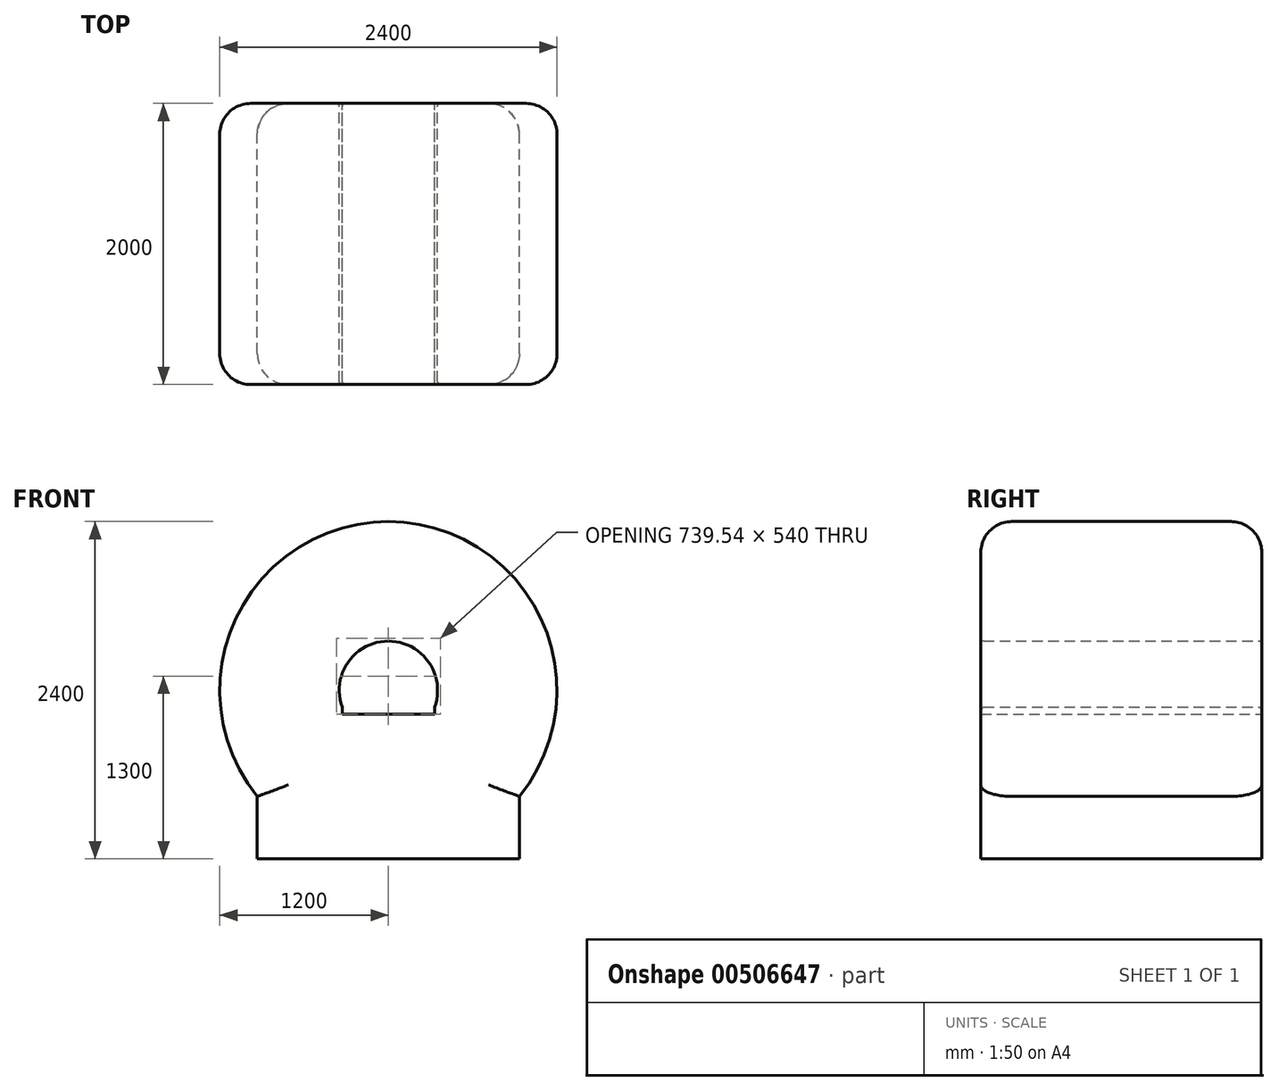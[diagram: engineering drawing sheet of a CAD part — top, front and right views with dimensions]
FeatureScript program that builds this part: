
annotation { "Feature Type Name" : "Feature", "Feature Type Description" : "" }
export const myFeature = defineFeature(function(context is Context, id is Id, definition is map)
    precondition{}
    {
        {
            var Q0;
            Q0=qCreatedBy(makeId("Front.planeOp"),FACE);
            var sketch = newSketch(context, id + "F0", { "sketchPlane" : qUnion([Q0])});
            skArc(sketch, "E0", {"start": v(932.57, -755.19) * mm, "mid": v(0, 1200) * mm, "end": v(-932.57, -755.19) * mm});
            skLineSegment(sketch, "E1", {"start": v(0, -1200) * mm, "end": v(0, -373.03) * mm, "construction": true});
            skLineSegment(sketch, "E2", {"start": v(0, -1200) * mm, "end": v(-932.57, -1200) * mm});
            skLineSegment(sketch, "E3", {"start": v(-932.57, -1200) * mm, "end": v(-932.57, -755.19) * mm});
            skLineSegment(sketch, "E4.MirrorCS", {"start": v(0, -1200) * mm, "end": v(932.57, -1200) * mm});
            skLineSegment(sketch, "E5.MirrorCS", {"start": v(932.57, -1200) * mm, "end": v(932.57, -755.19) * mm});
            skCircle(sketch, "E6", {"center": v(0, 0) * mm, "radius": 350 * mm});
            skSolve(sketch);
        }
        {
            var Q0;
            Q0 = qSketchRegion(id + "F0", true);
            extrude(context, id + "F1", {"entities" : qUnion([Q0]), "depth" : 2000 * mm});
        }
        {
            var Q0;
            Q0=makeQuery(id+"F1.opExtrude","CAP_EDGE",EDGE,{"disambiguationData":[OSD([sQuery(id+"F0.wireOp",EDGE,"E0")])],"isStart":false});
            var Q1;
            Q1=makeQuery(id+"F1.opExtrude","CAP_EDGE",EDGE,{"disambiguationData":[OSD([sQuery(id+"F0.wireOp",EDGE,"E0")])],"isStart":true});
            var Q2;
            Q2=makeQuery(id+"F1.opExtrude","CAP_EDGE",EDGE,{"disambiguationData":[OSD([sQuery(id+"F0.wireOp",EDGE,"E5.MirrorCS")])],"isStart":false});
            var Q3;
            Q3=makeQuery(id+"F1.opExtrude","CAP_EDGE",EDGE,{"disambiguationData":[OSD([sQuery(id+"F0.wireOp",EDGE,"E3")])],"isStart":false});
            var Q4;
            Q4=makeQuery(id+"F1.opExtrude","CAP_EDGE",EDGE,{"disambiguationData":[OSD([sQuery(id+"F0.wireOp",EDGE,"E5.MirrorCS")])],"isStart":true});
            var Q5;
            Q5=makeQuery(id+"F1.opExtrude","CAP_EDGE",EDGE,{"disambiguationData":[OSD([sQuery(id+"F0.wireOp",EDGE,"E3")])],"isStart":true});
            fillet(context, id + "F2", {"entities" : qUnion([Q0, Q1, Q2, Q3, Q4, Q5]), "radius" : 220 * mm, "tangentPropagation" : true, "allowEdgeOverflow" : false});
        }
        {
            var Q0;
            Q0=makeQuery(id+"F1.opExtrude","CAP_FACE",FACE,{"disambiguationData":[OSD([sQuery(id+"F0.wireOp",EDGE,"E0"),sQuery(id+"F0.wireOp",EDGE,"E2"),sQuery(id+"F0.wireOp",EDGE,"E3"),sQuery(id+"F0.wireOp",EDGE,"E4.MirrorCS"),sQuery(id+"F0.wireOp",EDGE,"E5.MirrorCS"),sQuery(id+"F0.wireOp",EDGE,"E6")])],"isStart":true});
            var sketch = newSketch(context, id + "F3", { "sketchPlane" : qUnion([Q0])});
            skLineSegment(sketch, "E7", {"start": v(0, 0) * mm, "end": v(0, -350) * mm, "construction": true});
            skLineSegment(sketch, "E8", {"start": v(0, -120) * mm, "end": v(-328.79, -120) * mm});
            skLineSegment(sketch, "E9", {"start": v(-328.79, -120) * mm, "end": v(-328.79, -170) * mm});
            skLineSegment(sketch, "E10", {"start": v(-328.79, -170) * mm, "end": v(0, -170) * mm});
            skLineSegment(sketch, "E11.MirrorCS", {"start": v(328.79, -170) * mm, "end": v(0, -170) * mm});
            skLineSegment(sketch, "E12.MirrorCS", {"start": v(328.79, -120) * mm, "end": v(328.79, -170) * mm});
            skLineSegment(sketch, "E13.MirrorCS", {"start": v(0, -120) * mm, "end": v(328.79, -120) * mm});
            skLineSegment(sketch, "E14", {"start": v(0, -120) * mm, "end": v(0, 350) * mm, "construction": true});
            skSolve(sketch);
        }
        {
            var Q0;
            Q0 = qSketchRegion(id + "F3", true);
            extrude(context, id + "F4", {"entities" : qUnion([Q0]), "operationType" : NewBodyOperationType.REMOVE, "endBound" : BoundingType.THROUGH_ALL, "oppositeDirection" : true, "depth" : 25 * mm});
        }
        {
            var Q0;
            Q0=makeQuery(id+"F1.opExtrude","CAP_FACE",FACE,{"disambiguationData":[OSD([sQuery(id+"F0.wireOp",EDGE,"E0"),sQuery(id+"F0.wireOp",EDGE,"E2"),sQuery(id+"F0.wireOp",EDGE,"E3"),sQuery(id+"F0.wireOp",EDGE,"E4.MirrorCS"),sQuery(id+"F0.wireOp",EDGE,"E5.MirrorCS"),sQuery(id+"F0.wireOp",EDGE,"E6")])],"isStart":true});
            var sketch = newSketch(context, id + "F5", { "sketchPlane" : qUnion([Q0])});
            skLineSegment(sketch, "E15", {"start": v(-305.94, -170) * mm, "end": v(305.94, -170) * mm});
            skLineSegment(sketch, "E16", {"start": v(0, -350) * mm, "end": v(287.25, -350) * mm});
            skLineSegment(sketch, "E17", {"start": v(287.25, -350) * mm, "end": v(305.94, -170) * mm});
            skLineSegment(sketch, "E18.MirrorCS", {"start": v(-287.25, -350) * mm, "end": v(-305.94, -170) * mm});
            skLineSegment(sketch, "E19.MirrorCS", {"start": v(0, -350) * mm, "end": v(-287.25, -350) * mm});
            skSolve(sketch);
        }
        {
            var Q0;
            Q0 = qSketchRegion(id + "F5", true);
            var Q1;
            Q1=makeQuery(id+"F1.opExtrude","CAP_FACE",FACE,{"disambiguationData":[OSD([sQuery(id+"F0.wireOp",EDGE,"E0"),sQuery(id+"F0.wireOp",EDGE,"E2"),sQuery(id+"F0.wireOp",EDGE,"E3"),sQuery(id+"F0.wireOp",EDGE,"E4.MirrorCS"),sQuery(id+"F0.wireOp",EDGE,"E5.MirrorCS"),sQuery(id+"F0.wireOp",EDGE,"E6")])],"isStart":false});
            extrude(context, id + "F6", {"entities" : qUnion([Q0]), "operationType" : NewBodyOperationType.ADD, "endBound" : BoundingType.UP_TO_SURFACE, "oppositeDirection" : true, "endBoundEntityFace" : qUnion([Q1]), "depth" : 25 * mm});
        }
        {
            var Q0;
            {var subQ0=sQuery(id+"F0.wireOp",EDGE,"E6");Q0=makeQuery(id+"F4.boolean.opBoolean","SPLIT",EDGE,{"disambiguationData":[TD([makeQuery(id+"F4.opExtrude","SWEPT_FACE",FACE,{"disambiguationData":[OSD([sQuery(id+"F3.wireOp",EDGE,"E9")])]})])],"derivedFrom":makeQuery(id+"F1.opExtrude","CAP_EDGE",EDGE,{"disambiguationData":[OSD([subQ0])],"isStart":true})});}
            var Q1;
            {var subQ0=sQuery(id+"F0.wireOp",EDGE,"E6");Q1=makeQuery(id+"F4.boolean.opBoolean","SPLIT",EDGE,{"disambiguationData":[TD([makeQuery(id+"F4.opExtrude","SWEPT_FACE",FACE,{"disambiguationData":[OSD([sQuery(id+"F3.wireOp",EDGE,"E9")])]})])],"derivedFrom":makeQuery(id+"F1.opExtrude","CAP_EDGE",EDGE,{"disambiguationData":[OSD([subQ0])],"isStart":false})});}
            fillet(context, id + "F7", {"entities" : qUnion([Q0, Q1]), "radius" : 20 * mm, "tangentPropagation" : true, "allowEdgeOverflow" : false});
        }
    });
